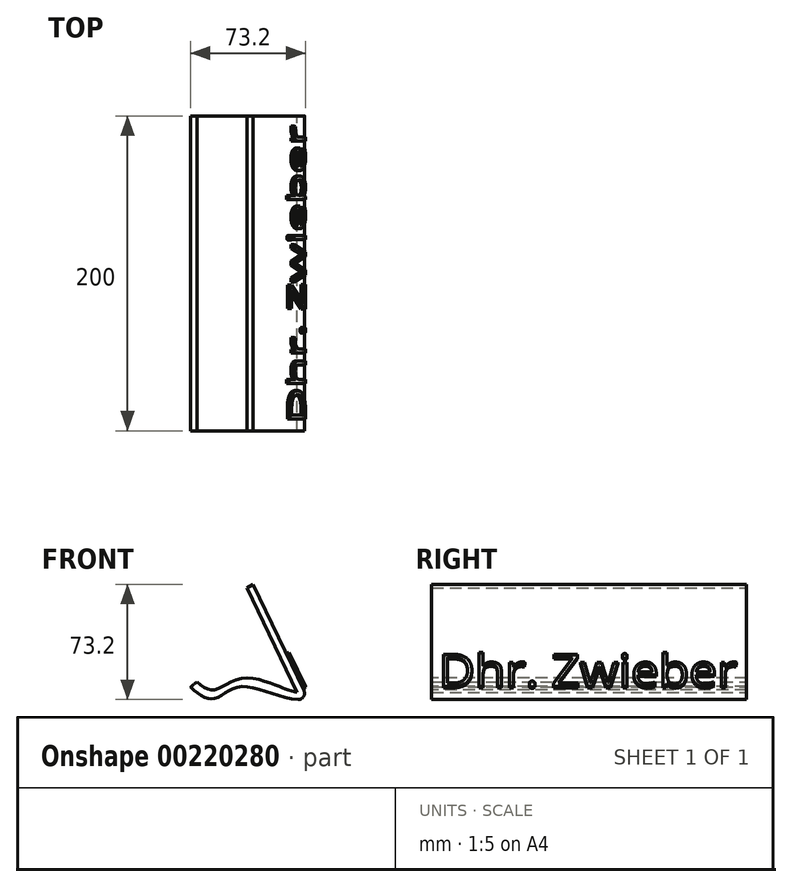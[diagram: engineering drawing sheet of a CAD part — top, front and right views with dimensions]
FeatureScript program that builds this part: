
annotation { "Feature Type Name" : "Feature", "Feature Type Description" : "" }
export const myFeature = defineFeature(function(context is Context, id is Id, definition is map)
    precondition{}
    {
        {
            var Q0;
            Q0=qCreatedBy(makeId("Front.planeOp"),FACE);
            var sketch = newSketch(context, id + "F0", { "sketchPlane" : qUnion([Q0])});
            skLineSegment(sketch, "E0", {"start": v(0, 42.9) * mm, "end": v(34.64, -29.75) * mm});
            skFitSpline(sketch, "E1", {"points": [v(34.64, -29.75) * mm, v(-7.47, -22.05) * mm, v(-25.18, -29.75) * mm, v(-39.9, -22.37) * mm], "startDerivative": vector(-86.01, -22.84) * mm, "endDerivative": vector(-53.05, 50.15) * mm});
            skFitSpline(sketch, "E2", {"points": [v(-35.65, -19.06) * mm, v(-24.6, -24.04) * mm, v(-6.85, -16.83) * mm, v(17.24, -22.37) * mm, v(33.37, -27.1) * mm], "startDerivative": vector(52.98, -50.89) * mm, "endDerivative": vector(143.66, -33.17) * mm});
            skFitSpline(sketch, "E3", {"points": [v(-35.65, -19.06) * mm, v(-39.9, -22.37) * mm], "startDerivative": vector(-3.69, -2.7) * mm, "endDerivative": vector(-3.69, -2.7) * mm});
            skLineSegment(sketch, "E4", {"start": v(27.7, -25.77) * mm, "end": v(-3.9, 40.52) * mm});
            skLineSegment(sketch, "E5", {"start": v(-3.9, 40.52) * mm, "end": v(0, 42.9) * mm});
            skSolve(sketch);
        }
        {
            var Q0;
            Q0 = qSketchRegion(id + "F0", true);
            extrude(context, id + "F1", {"entities" : qUnion([Q0]), "depth" : 100 * mm, "hasSecondDirection" : true, "secondDirectionOppositeDirection" : true, "secondDirectionDepth" : 100 * mm});
        }
        {
            var Q0;
            Q0=makeQuery(id+"F1.opExtrude","SWEPT_EDGE",EDGE,{"disambiguationData":[OSD([sQuery(id+"F0.wireOp",EDGE,"E0"),sQuery(id+"F0.wireOp",EDGE,"E1")])]});
            fillet(context, id + "F2", {"entities" : qUnion([Q0]), "radius" : 4 * mm, "tangentPropagation" : true, "allowEdgeOverflow" : false});
        }
        {
            var Q0;
            Q0=makeQuery(id+"F1.opExtrude","SWEPT_FACE",FACE,{"disambiguationData":[OSD([sQuery(id+"F0.wireOp",EDGE,"E0")])]});
            var sketch = newSketch(context, id + "F3", { "sketchPlane" : qUnion([Q0])});
            skText(sketch, "E6", { "text": "Dhr. Zwieber", "fontName": "OpenSans-Regular.ttf"});
            const initialGuessF3  = {"E6": [-0.0955, -0.03404, 1, 0, 0.02267]};
            skSetInitialGuess(sketch, initialGuessF3);
            skSolve(sketch);
        }
        {
            var Q0;
            Q0 = qSketchRegion(id + "F3", true);
            extrude(context, id + "F4", {"entities" : qUnion([Q0]), "operationType" : NewBodyOperationType.ADD, "depth" : 2 * mm});
        }
    });
